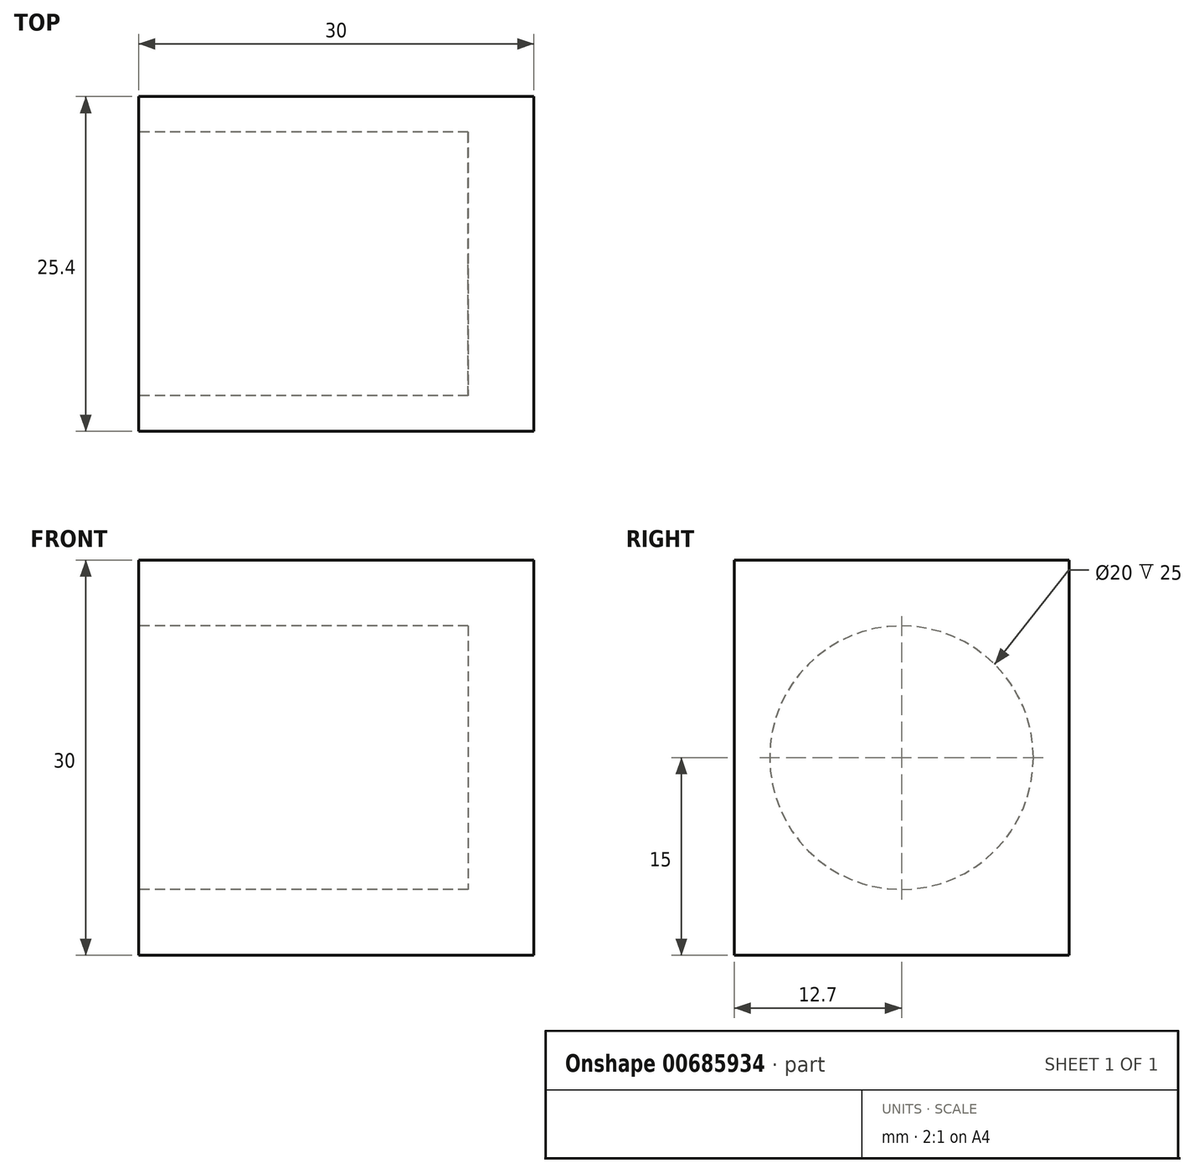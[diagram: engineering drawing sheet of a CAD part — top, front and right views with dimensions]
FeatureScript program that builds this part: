
annotation { "Feature Type Name" : "Feature", "Feature Type Description" : "" }
export const myFeature = defineFeature(function(context is Context, id is Id, definition is map)
    precondition{}
    {
        {
            var Q0;
            Q0=qCreatedBy(makeId("Front.planeOp"),FACE);
            var sketch = newSketch(context, id + "F0", { "sketchPlane" : qUnion([Q0])});
            skLineSegment(sketch, "E0.bottom", {"start": v(0, 0) * mm, "end": v(30, 0) * mm});
            skLineSegment(sketch, "E0.top", {"start": v(0, 30) * mm, "end": v(30, 30) * mm});
            skLineSegment(sketch, "E0.left", {"start": v(0, 0) * mm, "end": v(0, 30) * mm});
            skLineSegment(sketch, "E0.right", {"start": v(30, 0) * mm, "end": v(30, 30) * mm});
            skLineSegment(sketch, "E1.bottom", {"start": v(0, 0) * mm, "end": v(0, 0) * mm});
            skLineSegment(sketch, "E1.top", {"start": v(0, 0) * mm, "end": v(0, 0) * mm});
            skSolve(sketch);
        }
        {
            var Q0;
            Q0 = qSketchRegion(id + "F0", true);
            extrude(context, id + "F1", {"entities" : qUnion([Q0]), "depth" : 25.4 * mm, "offsetDistance" : 25.4 * mm});
        }
        {
            var Q0;
            Q0=makeQuery(id+"F1.opExtrude","SWEPT_FACE",FACE,{"disambiguationData":[OSD([sQuery(id+"F0.wireOp",EDGE,"E0.left")])]});
            var sketch = newSketch(context, id + "F2", { "sketchPlane" : qUnion([Q0])});
            skCircle(sketch, "E2", {"center": v(12.7, 15) * mm, "radius": 10 * mm});
            skPoint(sketch, "E2.centerSnap0", {"position": v(25.4, 15) * mm});
            skPoint(sketch, "E2.centerSnap1", {"position": v(12.7, 30) * mm});
            skSolve(sketch);
        }
        {
            var Q0;
            Q0 = qSketchRegion(id + "F2", true);
            extrude(context, id + "F3", {"entities" : qUnion([Q0]), "operationType" : NewBodyOperationType.REMOVE, "oppositeDirection" : true, "depth" : 25 * mm, "offsetDistance" : 25 * mm});
        }
    });
